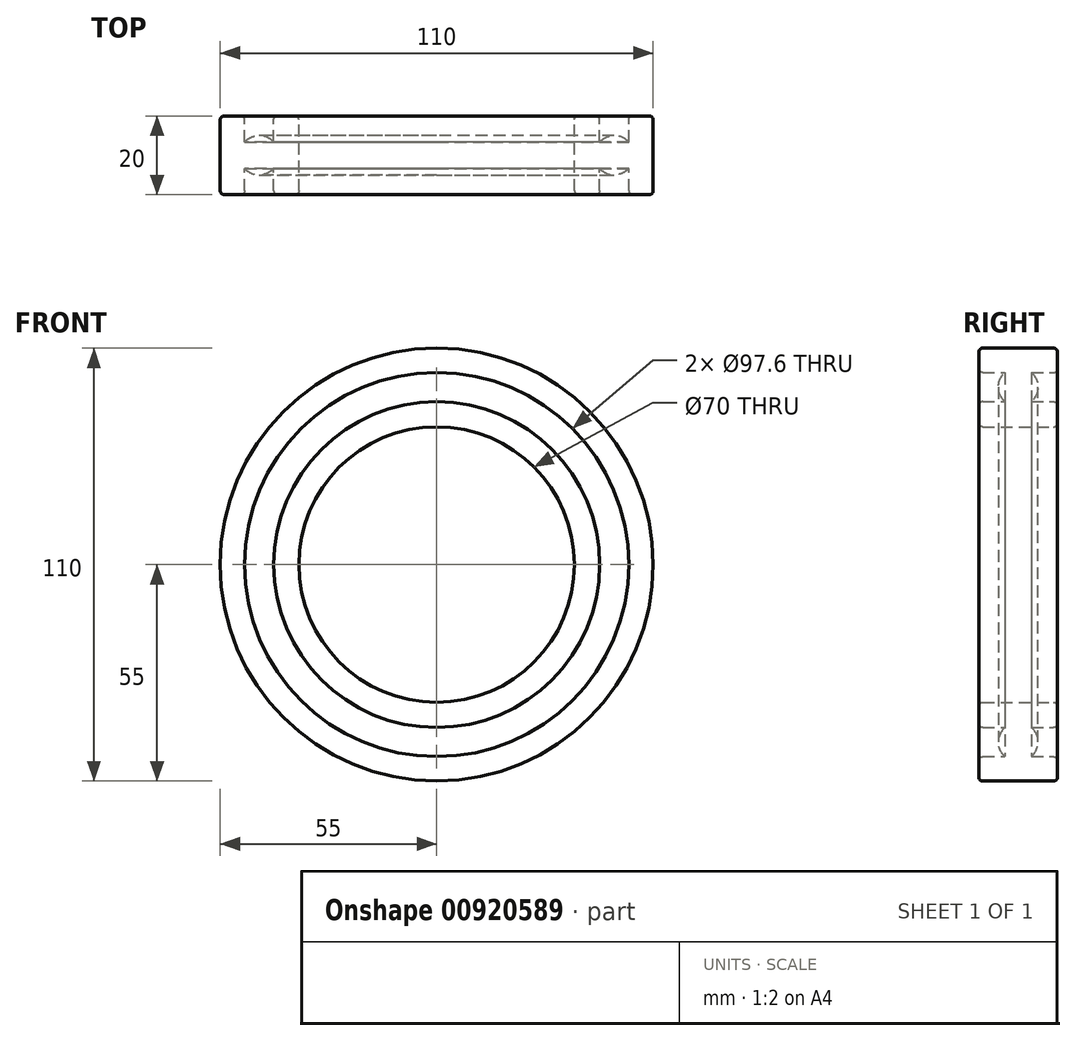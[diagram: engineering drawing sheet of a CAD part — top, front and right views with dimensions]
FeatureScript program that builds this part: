
annotation { "Feature Type Name" : "Feature", "Feature Type Description" : "" }
export const myFeature = defineFeature(function(context is Context, id is Id, definition is map)
    precondition{}
    {
        {
            var Q0;
            Q0=qCreatedBy(makeId("Front.planeOp"),FACE);
            var sketch = newSketch(context, id + "F0", { "sketchPlane" : qUnion([Q0])});
            skCircle(sketch, "E0", {"center": v(0, 0) * mm, "radius": 55 * mm});
            skCircle(sketch, "E1", {"center": v(0, 0) * mm, "radius": 35 * mm});
            skSolve(sketch);
        }
        {
            var Q0;
            Q0=makeQuery(id+"F0.imprint","IMPRINT",FACE,{"disambiguationData":[TD([[makeQuery(id+"F0.imprint","IMPRINT",EDGE,{"derivedFrom":sQuery(id+"F0.wireOp",EDGE,"E0")}),1.0]])]});
            extrude(context, id + "F1", {"entities" : qUnion([Q0]), "depth" : 20 * mm, "offsetDistance" : 25 * mm, "symmetric" : true});
        }
        {
            var Q0;
            Q0=qCreatedBy(makeId("Right.planeOp"),FACE);
            var sketch = newSketch(context, id + "F2", { "sketchPlane" : qUnion([Q0])});
            skLineSegment(sketch, "E2", {"start": v(0, 0) * mm, "end": v(32.98, 0) * mm, "construction": true});
            skLineSegment(sketch, "E3.bottom", {"start": v(-20, 48.8) * mm, "end": v(20, 48.8) * mm, "construction": true});
            skLineSegment(sketch, "E3.top", {"start": v(-20, 41.4) * mm, "end": v(20, 41.4) * mm, "construction": true});
            skLineSegment(sketch, "E3.left", {"start": v(-20, 48.8) * mm, "end": v(-20, 41.4) * mm});
            skLineSegment(sketch, "E3.right", {"start": v(20, 48.8) * mm, "end": v(20, 41.4) * mm});
            skArc(sketch, "E4", {"start": v(3.36, 41.4) * mm, "mid": v(5, 45.1) * mm, "end": v(3.36, 48.8) * mm});
            skLineSegment(sketch, "E5", {"start": v(0, 48.8) * mm, "end": v(0, 41.4) * mm, "construction": true});
            skArc(sketch, "E6.trimOffspring", {"start": v(-3.36, 48.8) * mm, "mid": v(-5, 45.1) * mm, "end": v(-3.36, 41.4) * mm});
            skLineSegment(sketch, "E7", {"start": v(-3.36, 48.8) * mm, "end": v(-20, 48.8) * mm});
            skLineSegment(sketch, "E8", {"start": v(-20, 41.4) * mm, "end": v(-3.36, 41.4) * mm});
            skLineSegment(sketch, "E9", {"start": v(3.36, 48.8) * mm, "end": v(20, 48.8) * mm});
            skLineSegment(sketch, "E10", {"start": v(3.36, 41.4) * mm, "end": v(20, 41.4) * mm});
            skSolve(sketch);
        }
        {
            var Q0;
            Q0=makeQuery(id+"F2.imprint","IMPRINT",FACE,{"disambiguationData":[TD([[makeQuery(id+"F2.imprint","IMPRINT",EDGE,{"derivedFrom":sQuery(id+"F2.wireOp",EDGE,"E3.left")}),1.0]])]});
            var Q1;
            Q1=makeQuery(id+"F2.imprint","IMPRINT",FACE,{"disambiguationData":[TD([[makeQuery(id+"F2.imprint","IMPRINT",EDGE,{"derivedFrom":sQuery(id+"F2.wireOp",EDGE,"E3.right")}),-1.0]])]});
            var Q2;
            Q2=sQuery(id+"F2.wireOp",EDGE,"E2");
            revolve(context, id + "F3", {"operationType" : NewBodyOperationType.REMOVE, "surfaceOperationType" : NewSurfaceOperationType.NEW, "entities" : qUnion([Q0, Q1]), "axis" : qUnion([Q2]), "revolveType" : RevolveType.FULL, "oppositeDirection" : true});
        }
        {
            var Q0;
            Q0=makeQuery(id+"F1.opExtrude","CAP_EDGE",EDGE,{"disambiguationData":[OSD([sQuery(id+"F0.wireOp",EDGE,"E0")])],"isStart":true});
            var Q1;
            Q1=makeQuery(id+"F1.opExtrude","CAP_EDGE",EDGE,{"disambiguationData":[OSD([sQuery(id+"F0.wireOp",EDGE,"E0")])],"isStart":false});
            var Q2;
            Q2=makeQuery(id+"F1.opExtrude","CAP_EDGE",EDGE,{"disambiguationData":[OSD([sQuery(id+"F0.wireOp",EDGE,"E1")])],"isStart":true});
            var Q3;
            Q3=makeQuery(id+"F1.opExtrude","CAP_EDGE",EDGE,{"disambiguationData":[OSD([sQuery(id+"F0.wireOp",EDGE,"E1")])],"isStart":false});
            var Q4;
            Q4=makeQuery(id+"F3.boolean.opBoolean","INTERSECT",EDGE,{"derivedFrom":[makeQuery(id+"F1.opExtrude","CAP_FACE",FACE,{"disambiguationData":[OSD([sQuery(id+"F0.wireOp",EDGE,"E0"),sQuery(id+"F0.wireOp",EDGE,"E1")])],"isStart":false}),makeQuery(id+"F3.opRevolve","SWEPT_FACE",FACE,{"disambiguationData":[OSD([sQuery(id+"F2.wireOp",EDGE,"E7")])]})]});
            var Q5;
            Q5=makeQuery(id+"F3.boolean.opBoolean","INTERSECT",EDGE,{"derivedFrom":[makeQuery(id+"F1.opExtrude","CAP_FACE",FACE,{"disambiguationData":[OSD([sQuery(id+"F0.wireOp",EDGE,"E0"),sQuery(id+"F0.wireOp",EDGE,"E1")])],"isStart":false}),makeQuery(id+"F3.opRevolve","SWEPT_FACE",FACE,{"disambiguationData":[OSD([sQuery(id+"F2.wireOp",EDGE,"E8")])]})]});
            var Q6;
            Q6=makeQuery(id+"F3.boolean.opBoolean","INTERSECT",EDGE,{"derivedFrom":[makeQuery(id+"F1.opExtrude","CAP_FACE",FACE,{"disambiguationData":[OSD([sQuery(id+"F0.wireOp",EDGE,"E0"),sQuery(id+"F0.wireOp",EDGE,"E1")])],"isStart":true}),makeQuery(id+"F3.opRevolve","SWEPT_FACE",FACE,{"disambiguationData":[OSD([sQuery(id+"F2.wireOp",EDGE,"E9")])]})]});
            var Q7;
            Q7=makeQuery(id+"F3.boolean.opBoolean","INTERSECT",EDGE,{"derivedFrom":[makeQuery(id+"F1.opExtrude","CAP_FACE",FACE,{"disambiguationData":[OSD([sQuery(id+"F0.wireOp",EDGE,"E0"),sQuery(id+"F0.wireOp",EDGE,"E1")])],"isStart":true}),makeQuery(id+"F3.opRevolve","SWEPT_FACE",FACE,{"disambiguationData":[OSD([sQuery(id+"F2.wireOp",EDGE,"E10")])]})]});
            fillet(context, id + "F4", {"entities" : qUnion([Q0, Q1, Q2, Q3, Q4, Q5, Q6, Q7]), "radius" : 1 * mm, "tangentPropagation" : true, "allowEdgeOverflow" : false});
        }
    });
